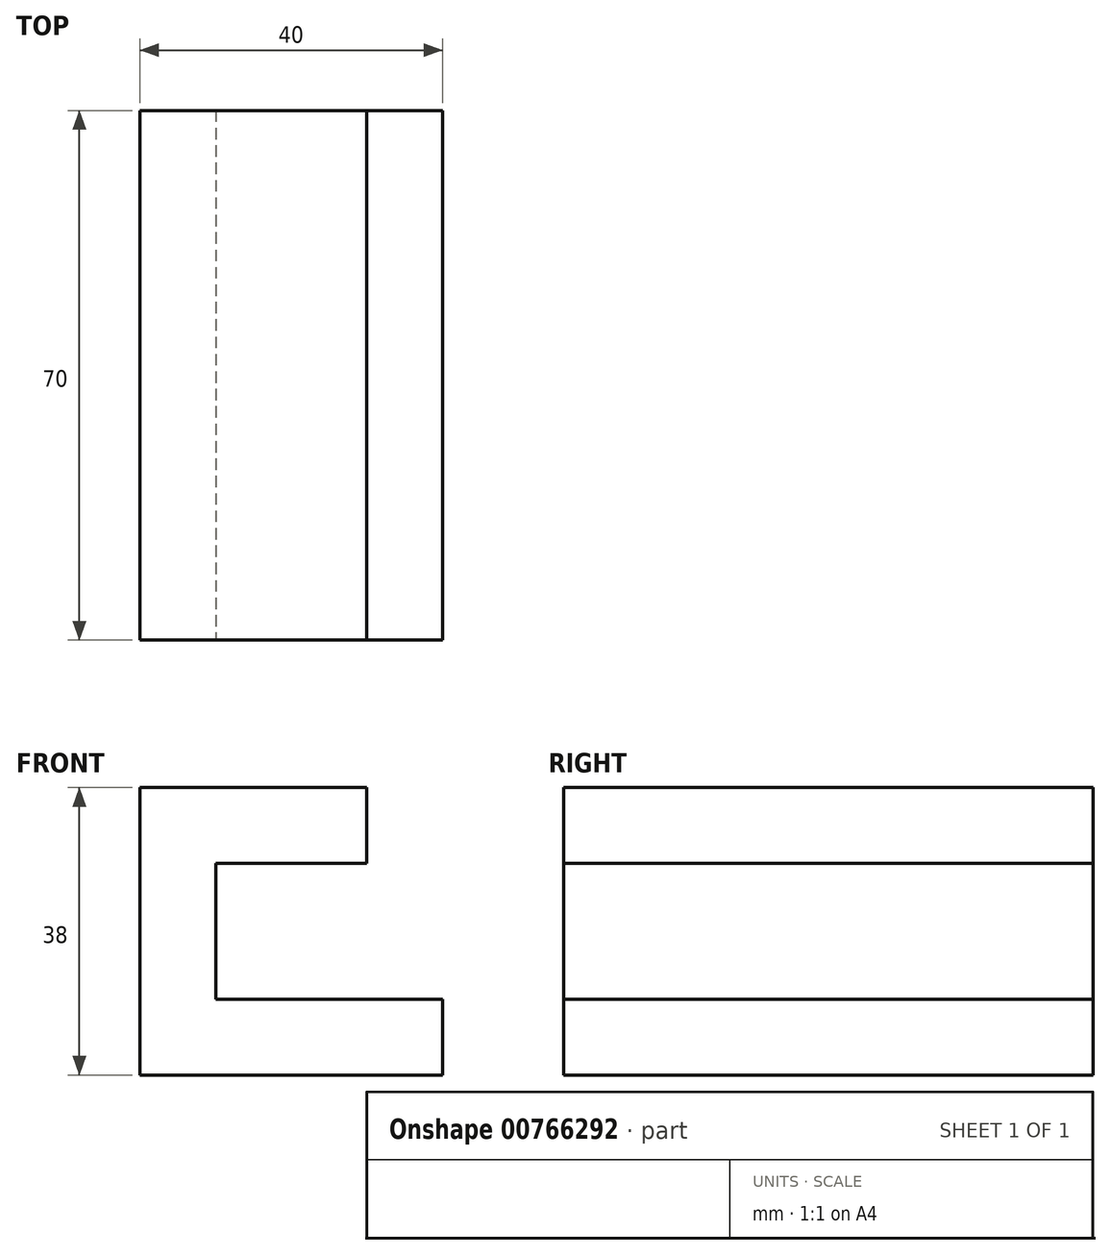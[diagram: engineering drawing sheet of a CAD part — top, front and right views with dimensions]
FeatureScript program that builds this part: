
annotation { "Feature Type Name" : "Feature", "Feature Type Description" : "" }
export const myFeature = defineFeature(function(context is Context, id is Id, definition is map)
    precondition{}
    {
        {
            var Q0;
            Q0=qCreatedBy(makeId("Front.planeOp"),FACE);
            var sketch = newSketch(context, id + "F0", { "sketchPlane" : qUnion([Q0])});
            skLineSegment(sketch, "E0.bottom", {"start": v(15, 38) * mm, "end": v(-15, 38) * mm});
            skLineSegment(sketch, "E0.top", {"start": v(15, 0) * mm, "end": v(-15, 0) * mm});
            skLineSegment(sketch, "E0.left", {"start": v(15, 38) * mm, "end": v(15, 0) * mm});
            skLineSegment(sketch, "E0.right", {"start": v(-15, 38) * mm, "end": v(-15, 0) * mm});
            skLineSegment(sketch, "E1.bottom", {"start": v(-5, 28) * mm, "end": v(15, 28) * mm});
            skLineSegment(sketch, "E1.top", {"start": v(-5, 10) * mm, "end": v(15, 10) * mm});
            skLineSegment(sketch, "E1.left", {"start": v(-5, 28) * mm, "end": v(-5, 10) * mm});
            skLineSegment(sketch, "E1.right", {"start": v(15, 28) * mm, "end": v(15, 10) * mm});
            skLineSegment(sketch, "E2.bottom", {"start": v(15, 10) * mm, "end": v(25, 10) * mm});
            skLineSegment(sketch, "E2.top", {"start": v(15, 0) * mm, "end": v(25, 0) * mm});
            skLineSegment(sketch, "E2.left", {"start": v(15, 10) * mm, "end": v(15, 0) * mm});
            skLineSegment(sketch, "E2.right", {"start": v(25, 10) * mm, "end": v(25, 0) * mm});
            skSolve(sketch);
        }
        {
            var Q0;
            Q0=makeQuery(id+"F0.imprint","IMPRINT",FACE,{"disambiguationData":[TD([[makeQuery(id+"F0.imprint","IMPRINT",EDGE,{"derivedFrom":sQuery(id+"F0.wireOp",EDGE,"E0.bottom")}),1.0]])]});
            var Q1;
            Q1=makeQuery(id+"F0.imprint","IMPRINT",FACE,{"disambiguationData":[TD([[makeQuery(id+"F0.imprint","IMPRINT",EDGE,{"derivedFrom":sQuery(id+"F0.wireOp",EDGE,"E2.bottom")}),-1.0]])]});
            extrude(context, id + "F1", {"entities" : qUnion([Q0, Q1]), "endBound" : BoundingType.SYMMETRIC, "oppositeDirection" : true, "depth" : 70 * mm, "offsetDistance" : 25 * mm});
        }
    });
